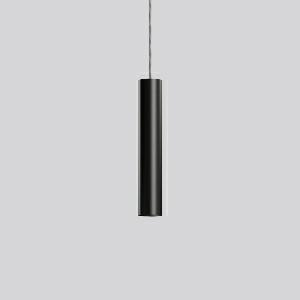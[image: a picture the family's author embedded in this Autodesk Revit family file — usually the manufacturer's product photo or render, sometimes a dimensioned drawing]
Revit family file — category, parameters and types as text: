
# Revit family: deecos_p_micro_911491_003_52a3
name_source: partatom
category: Lighting Fixtures
units: mm (PartAtom-declared; Revit-internal decimal feet)

## family parameters
Cut with Voids When Loaded = No
Host = Face
Light Source = No
Part Type = Normal
Room Calculation Point = No
Round Connector Dimension = Use Diameter
Shared = No

## types (1)
- DEECOS P micro (1 x LED Modul 927, 1600 lm, 2700)
    Apparent Load = 16 VA
    CIE Flux Codes = 98 100 100 100 100
    Color Rendering = 92
    Color Temperature = 2700
    Default Elevation = 1800 mm
    Description = Series: DEECOS P micro
Cylindrical pendant luminaire. Housing: die-cast aluminium, powder-coated. Canopy made of powder-coated sheet steel with magnetic attachment. Optical assembly with reflector made of MIRO-Silver with 98% total light reflection for outstanding efficiency - can be changed without tools. Black plastic ring and recessed LED to prevent glare from the side. Best colour rendering index Ra>90. Transparent suspension cable 3 m, can be shortened. High quality converter without flickering and stroboscopic effect. 
Colour: deep black, matt (RAL 9005)
Diameter: 60 mm
Height: 340 mm
Suspension length: 3000 mm
Lamp: LED
Socket: without socket
Colour temperature: 2700K
Colour rendering index (CRI): 92
System power: 16 W
Rated luminous flux: 1600 lm
Luminous efficiency: 100 lm/W
Control gear: Regulated power supply
Protection class: I
Type of protection: IP 20
    Height = 340 mm
    Lamp = 1 x LED Modul 927
    Lamp Light Flux = 1600 lm
    Lamp count = 1
    Length = 60 mm  [stored 0.19685 ft]
    Lifetime = 50000 h
    Luminous efficacy = 100 lm/W
    Manufacturer = RZB
    ModVariant = No
    Model = 911491.003
    Mounting Place = Ceiling
    Mounting Type = Pendant
    Number of Poles = 1
    OnlyDefault = Yes
    Power Factor = 1
    Product Name = DEECOS P micro
    Product group = Pendant luminaires
    ProductGroupID = 902
    Protection Class = Protection class I
    Protection Degree = Degree of protection
    RLX_Detail_Level = 1
    RLX_Emergency_Light_Flux = 0 lm
    RLX_Emergency_Type = 0
    RLX_Emergency_Type_DB = No
    RlxData = <blob elided: 32093 chars, md5=cef99cc6>
    Socket = socket
    Standby Power = 0 W
    System Light Flux = 1600 lm
    System Power = 16 W
    Type Comments = Product without accessories
    Type Image = 911491.003.jpg
    URL = http://relux.com
    VarID = ---
    Voltage = 0 V
    Weight = 0.00 kg
    Width = 0 mm  [stored 0 ft]

note: [stored X ft] marks values corroborated as IEEE doubles in the binary element streams (Revit-internal decimal feet)

## geometry (parser evidence)
native form markers: Blend x4, Sweep x11
no freeform markers — native parametric forms only
